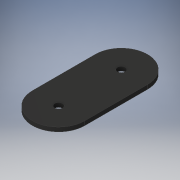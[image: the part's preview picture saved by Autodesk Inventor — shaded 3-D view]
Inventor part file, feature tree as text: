
AUTODESK INVENTOR PART (.ipt)
format: ipt  version: 2019 (Build 230136000, 136)  size: 126,976 bytes
history: native  units: mm
features: extrude x1, sketch x1
ambient origin geometry x8: Origin, YZ Plane, XZ Plane, XY Plane, X Axis, Y Axis, Z Axis, Center Point
bodies: Solid1 (feature_tree)
feature tree (2):
  extrude  "Extrusion1"  Depth=20.0mm
  sketch  "Sketch1"  dims[d15=1.5875mm d16=0.0mm d25=13.0mm d26=14.0mm d30=5.0mm d31=5.0mm d32=3.0mm d33=20.0mm]
